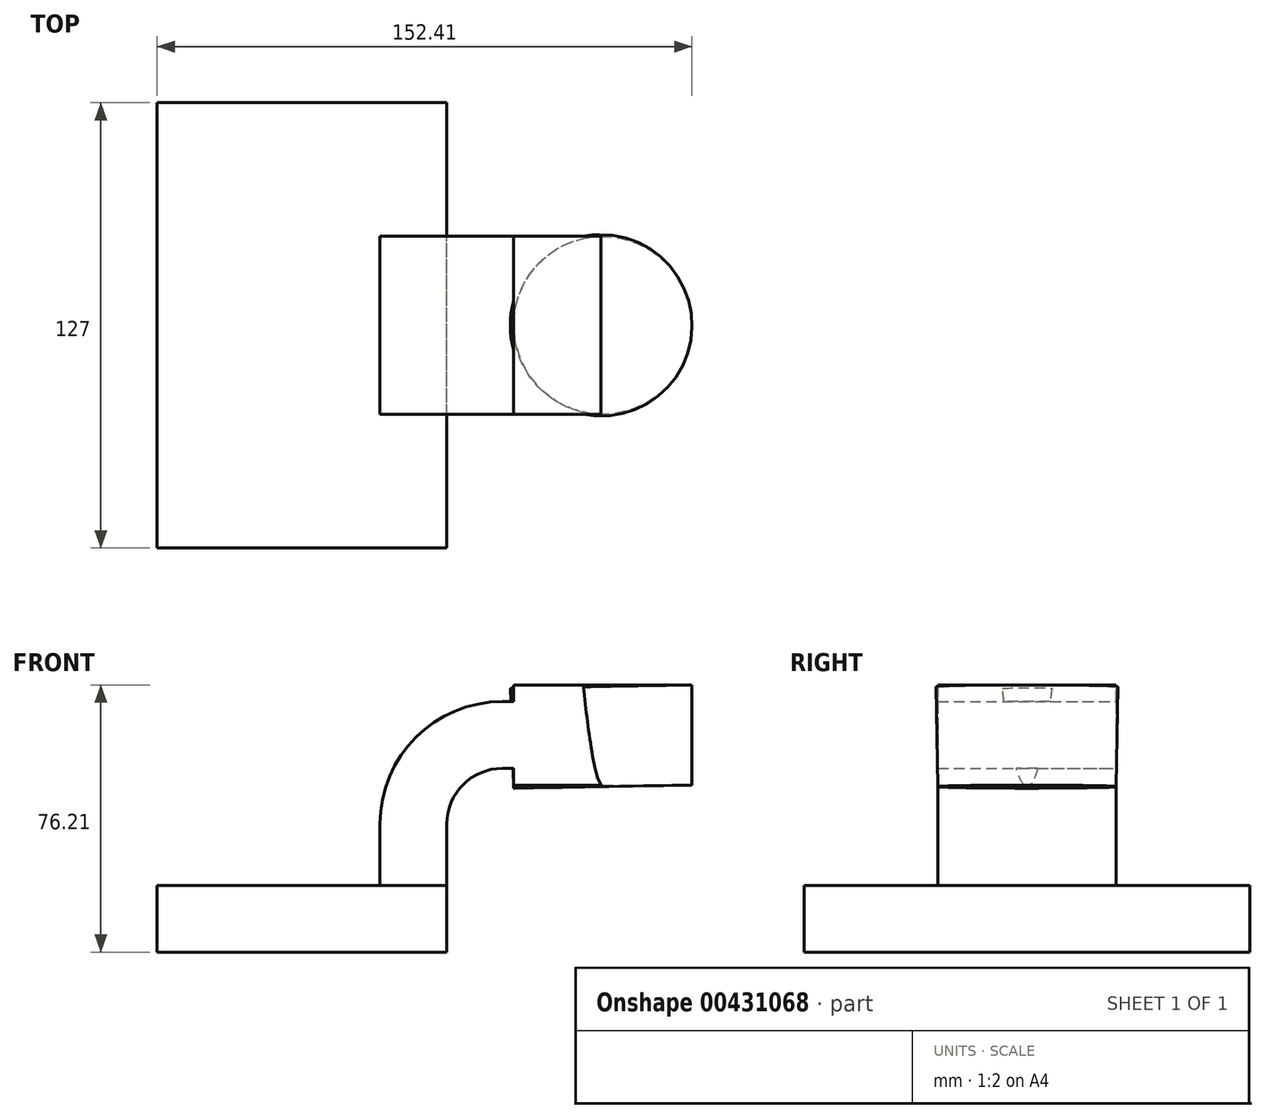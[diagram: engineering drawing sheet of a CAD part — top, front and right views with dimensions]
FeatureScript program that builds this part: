
annotation { "Feature Type Name" : "Feature", "Feature Type Description" : "" }
export const myFeature = defineFeature(function(context is Context, id is Id, definition is map)
    precondition{}
    {
        {
            var Q0;
            Q0=qCreatedBy(makeId("Front.planeOp"),FACE);
            var sketch = newSketch(context, id + "F0", { "sketchPlane" : qUnion([Q0])});
            skLineSegment(sketch, "E0.bottom", {"start": v(-41.28, -9.53) * mm, "end": v(41.28, -9.53) * mm});
            skLineSegment(sketch, "E0.top", {"start": v(-41.28, 9.52) * mm, "end": v(41.28, 9.52) * mm});
            skLineSegment(sketch, "E0.left", {"start": v(-41.27, -9.53) * mm, "end": v(-41.28, 9.52) * mm});
            skLineSegment(sketch, "E0.right", {"start": v(41.28, -9.53) * mm, "end": v(41.28, 9.52) * mm});
            skPoint(sketch, "E0.middle", {"position": v(0, 0) * mm});
            skLineSegment(sketch, "E1.bottom", {"start": v(111.12, 38.1) * mm, "end": v(60.32, 38.1) * mm});
            skLineSegment(sketch, "E1.top", {"start": v(111.12, 66.67) * mm, "end": v(60.33, 66.67) * mm});
            skLineSegment(sketch, "E1.left", {"start": v(111.12, 38.1) * mm, "end": v(111.12, 66.67) * mm});
            skLineSegment(sketch, "E1.right", {"start": v(60.33, 38.1) * mm, "end": v(60.33, 66.67) * mm});
            skPoint(sketch, "E1.middle", {"position": v(85.72, 52.39) * mm});
            skLineSegment(sketch, "E2", {"start": v(41.27, 9.52) * mm, "end": v(41.27, 27) * mm});
            skArc(sketch, "E3", {"start": v(41.27, 27) * mm, "mid": v(45.92, 38.23) * mm, "end": v(57.15, 42.88) * mm});
            skLineSegment(sketch, "E4", {"start": v(57.15, 42.88) * mm, "end": v(85.23, 42.88) * mm});
            skLineSegment(sketch, "E5.0", {"start": v(57.15, 61.93) * mm, "end": v(85.23, 61.93) * mm});
            skArc(sketch, "E5.1", {"start": v(22.22, 27) * mm, "mid": v(32.45, 51.7) * mm, "end": v(57.15, 61.93) * mm});
            skLineSegment(sketch, "E5.2", {"start": v(22.22, 9.52) * mm, "end": v(22.22, 27) * mm});
            skLineSegment(sketch, "E6", {"start": v(85.72, 38.1) * mm, "end": v(85.23, 66.67) * mm});
            skFitSpline(sketch, "E7", {"points": [v(-41.28, 9.53) * mm, v(57.15, 61.93) * mm], "startDerivative": vector(55.54, 96.36) * mm, "endDerivative": vector(116.63, -28.03) * mm});
            skSolve(sketch);
        }
        {
            var Q0;
            Q0=makeQuery(id+"F0.imprint","IMPRINT",FACE,{"disambiguationData":[TD([[makeQuery(id+"F0.imprint","IMPRINT",EDGE,{"derivedFrom":sQuery(id+"F0.wireOp",EDGE,"E0.bottom")}),1.0]])]});
            extrude(context, id + "F1", {"entities" : qUnion([Q0]), "endBound" : BoundingType.SYMMETRIC, "depth" : 127 * mm});
        }
        {
            var Q0;
            {var subQ1=sQuery(id+"F0.wireOp",EDGE,"E2");Q0=makeQuery(id+"F0.imprint","IMPRINT",FACE,{"disambiguationData":[TD([[makeQuery(id+"F0.imprint","IMPRINT",EDGE,{"derivedFrom":subQ1}),1.0]])]});}
            var Q1;
            {var subQ6=sQuery(id+"F0.wireOp",EDGE,"E6");Q1=makeQuery(id+"F0.imprint","IMPRINT",FACE,{"disambiguationData":[TD([[makeQuery(id+"F0.imprint","IMPRINT",EDGE,{"derivedFrom":subQ6}),1.0]])]});}
            extrude(context, id + "F2", {"entities" : qUnion([Q0, Q1]), "endBound" : BoundingType.SYMMETRIC, "depth" : 50.8 * mm});
        }
        {
            var Q0;
            Q0=makeQuery(id+"F0.imprint","IMPRINT",FACE,{"disambiguationData":[TD([[makeQuery(id+"F0.imprint","IMPRINT",EDGE,{"derivedFrom":sQuery(id+"F0.wireOp",EDGE,"E5.1")}),1.0]])]});
            extrude(context, id + "F3", {"entities" : qUnion([Q0]), "endBound" : BoundingType.SYMMETRIC, "depth" : 15.88 * mm});
        }
        {
            var Q0;
            {var subQ0=sQuery(id+"F0.wireOp",EDGE,"E1.left");Q0=makeQuery(id+"F0.imprint","IMPRINT",FACE,{"disambiguationData":[TD([[makeQuery(id+"F0.imprint","IMPRINT",EDGE,{"derivedFrom":subQ0}),1.0]])]});}
            var Q1;
            Q1=sQuery(id+"F0.wireOp",EDGE,"E6");
            revolve(context, id + "F4", {"operationType" : NewBodyOperationType.ADD, "entities" : qUnion([Q0]), "axis" : qUnion([Q1]), "revolveType" : RevolveType.FULL});
        }
    });
